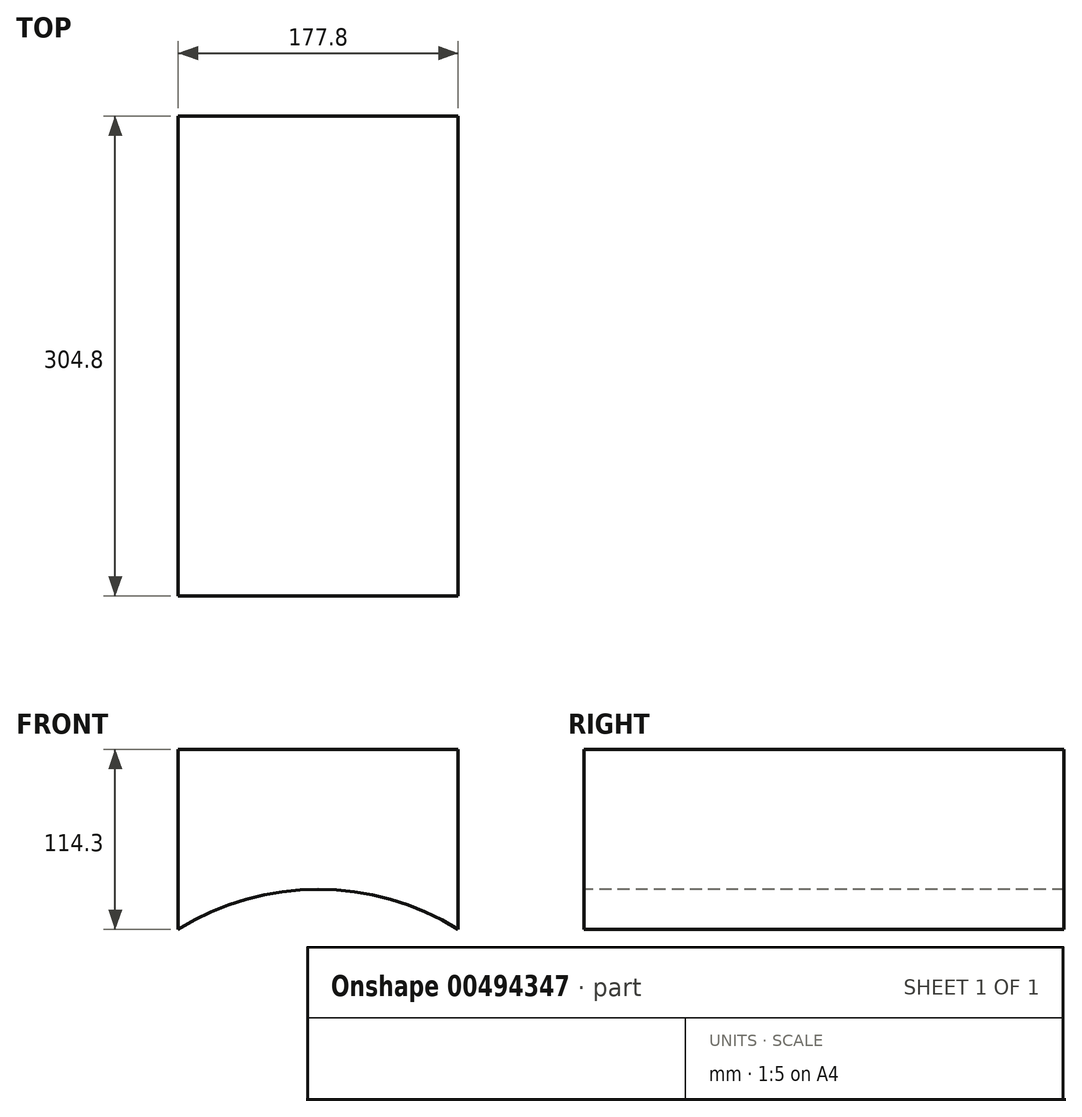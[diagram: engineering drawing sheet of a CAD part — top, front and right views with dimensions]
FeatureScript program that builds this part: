
annotation { "Feature Type Name" : "Feature", "Feature Type Description" : "" }
export const myFeature = defineFeature(function(context is Context, id is Id, definition is map)
    precondition{}
    {
        {
            var Q0;
            Q0=qCreatedBy(makeId("Front.planeOp"),FACE);
            var sketch = newSketch(context, id + "F0", { "sketchPlane" : qUnion([Q0])});
            skArc(sketch, "E0", {"start": v(0, 25.4) * mm, "mid": v(-46.23, 18.93) * mm, "end": v(-88.9, 0) * mm});
            skLineSegment(sketch, "E1", {"start": v(-88.9, 0) * mm, "end": v(-88.9, 114.3) * mm});
            skLineSegment(sketch, "E2", {"start": v(-88.9, 114.3) * mm, "end": v(0, 114.3) * mm});
            skLineSegment(sketch, "E3", {"start": v(0, 114.3) * mm, "end": v(0, 25.4) * mm});
            skSolve(sketch);
        }
        {
            var Q0;
            Q0 = qSketchRegion(id + "F0", true);
            extrude(context, id + "F1", {"entities" : qUnion([Q0]), "oppositeDirection" : true, "depth" : 304.8 * mm});
        }
        {
            var Q0;
            Q0=makeQuery(id+"F1.opExtrude","SWEPT_BODY",BODY,{"disambiguationData":[OSD([sQuery(id+"F0.wireOp",EDGE,"E0"),sQuery(id+"F0.wireOp",EDGE,"E1"),sQuery(id+"F0.wireOp",EDGE,"E2"),sQuery(id+"F0.wireOp",EDGE,"E3")])]});
            var Q1;
            Q1=qCreatedBy(makeId("Right.planeOp"),FACE);
            mirror(context, id + "F2", {"operationType" : NewBodyOperationType.ADD, "entities" : qUnion([Q0]), "mirrorPlane" : qUnion([Q1])});
        }
    });
